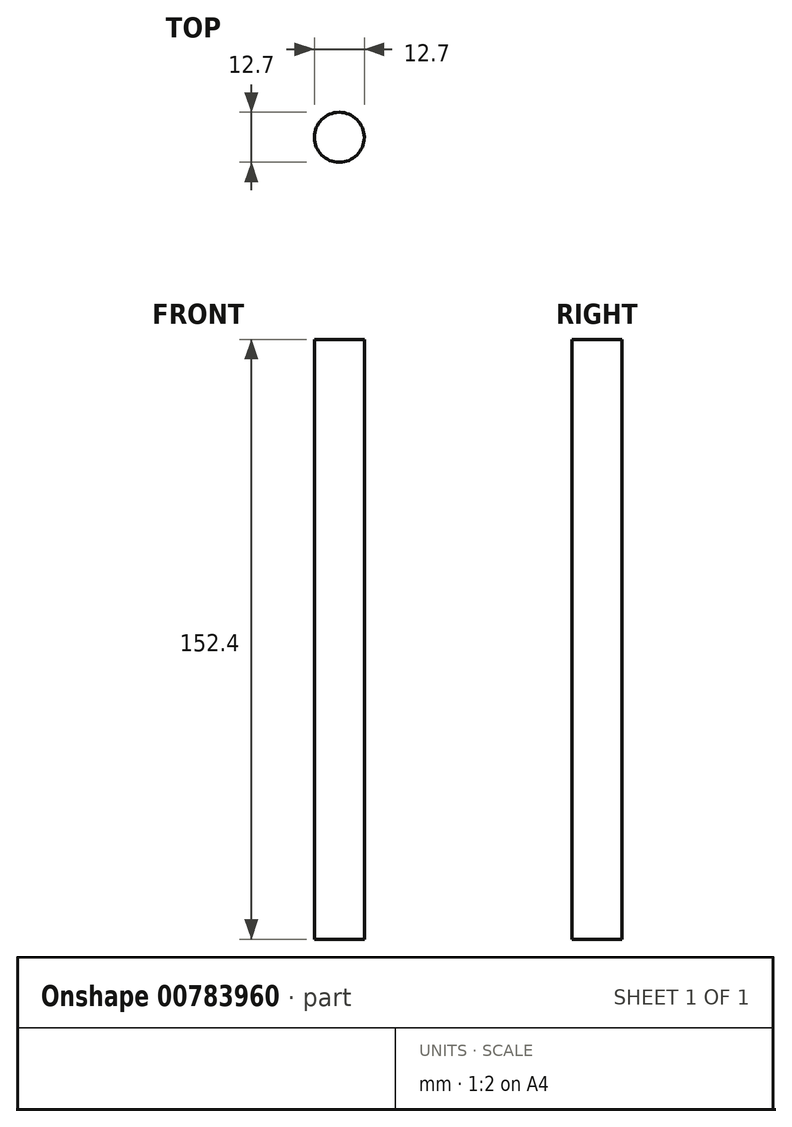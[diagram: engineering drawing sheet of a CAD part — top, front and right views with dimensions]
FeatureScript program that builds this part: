
annotation { "Feature Type Name" : "Feature", "Feature Type Description" : "" }
export const myFeature = defineFeature(function(context is Context, id is Id, definition is map)
    precondition{}
    {
        {
            var Q0;
            Q0=qCreatedBy(makeId("Top.planeOp"),FACE);
            var sketch = newSketch(context, id + "F0", { "sketchPlane" : qUnion([Q0])});
            skCircle(sketch, "E0", {"center": v(0, -7.42) * mm, "radius": 6.35 * mm});
            skSolve(sketch);
        }
        {
            var Q0;
            Q0 = qSketchRegion(id + "F0", true);
            extrude(context, id + "F1", {"entities" : qUnion([Q0]), "depth" : 152.4 * mm, "offsetDistance" : 25.4 * mm});
        }
    });
